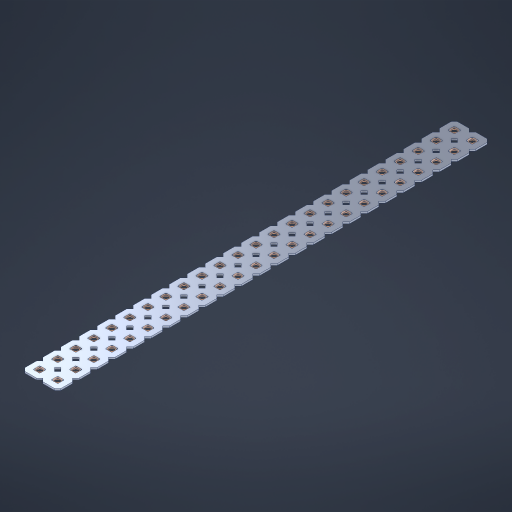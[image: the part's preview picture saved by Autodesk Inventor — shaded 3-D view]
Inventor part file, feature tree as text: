
AUTODESK INVENTOR PART (.ipt)
format: ipt  version: 2023 (Build 270158000, 158)  size: 814,080 bytes
history: native  units: in
note: dims shown in document units (in); Inventor stores cm internally (conversion verified against a paired STEP export)
features: other x49, extrude x47, sketch x2, pattern_linear x1
ambient origin geometry x8: Origin, YZ Plane, XZ Plane, XY Plane, X Axis, Y Axis, Z Axis, Center Point
bodies: Solid1 (feature_tree), Body (feature_tree)
feature tree (99):
  pattern_linear  "Rectangular Pattern1"  Spacing1=0.09in  [1 undecoded]
  sketch  "Sketch1"  dims[d1=0.5in]
  sketch  "Sketch2"  dims[d2=0.182in d3=0.09in d4=0.09in d5=0.09in d6=0.09in d7=0.09in d8=0.09in d9=0.09in d10=0.09in d11=0.02in d13=0.0in d14=0.172in d15=0.0625in d16=0.0in d19=0.5in d22=0.5in]
  other  "Srf1"
  other  "Srf126"
  other  "Srf127"
  other  "Srf128"
  other  "Srf129"
  other  "Srf130"
  other  "Srf131"
  other  "Srf250"
  other  "Srf251"
  other  "Srf252"
  other  "Srf253"
  other  "Srf254"
  other  "Srf255"
  other  "Srf256"
  other  "Srf257"
  other  "Srf258"
  other  "Srf259"
  other  "Srf260"
  other  "Srf261"
  other  "Srf262"
  other  "Srf263"
  other  "Srf264"
  other  "Srf265"
  other  "Srf266"
  other  "Srf268"
  other  "Srf269"
  other  "Srf270"
  other  "Srf271"
  other  "Srf272"
  other  "Srf273"
  other  "Srf274"
  other  "Srf275"
  other  "Srf276"
  other  "Srf277"
  other  "Srf278"
  other  "Srf279"
  other  "Srf280"
  other  "Srf281"
  other  "Srf282"
  other  "Srf283"
  other  "Srf284"
  other  "Srf285"
  other  "Srf286"
  other  "Srf287"
  other  "Srf288"
  other  "Srf289"
  other  "Srf290"
  other  "Srf291"
  other  "Circle"
  extrude  "ExtrusionSrf126"  Depth=0.09in
  extrude  "ExtrusionSrf127"  Depth=0.09in
  extrude  "ExtrusionSrf128"  Depth=0.09in
  extrude  "ExtrusionSrf129"  Depth=0.09in
  extrude  "ExtrusionSrf130"  Depth=0.09in
  extrude  "ExtrusionSrf131"  Depth=0.09in
  extrude  "ExtrusionSrf250"  Depth=0.09in
  extrude  "ExtrusionSrf251"  Depth=0.02in
  extrude  "ExtrusionSrf252"  TaperAngle=0.0deg  [1 undecoded]
  extrude  "ExtrusionSrf253"  Depth=0.5in
  extrude  "ExtrusionSrf254"  Depth=0.5in TaperAngle=0.0deg
  extrude  "ExtrusionSrf255"  Depth=0.5in
  extrude  "ExtrusionSrf256"  Depth=0.5in
  extrude  "ExtrusionSrf257"  [1 undecoded]
  extrude  "ExtrusionSrf258"  [1 undecoded]
  extrude  "ExtrusionSrf259"  [1 undecoded]
  extrude  "ExtrusionSrf260"  [1 undecoded]
  extrude  "ExtrusionSrf261"  [1 undecoded]
  extrude  "ExtrusionSrf262"  [1 undecoded]
  extrude  "ExtrusionSrf263"  [1 undecoded]
  extrude  "ExtrusionSrf264"  [1 undecoded]
  extrude  "ExtrusionSrf265"  [1 undecoded]
  extrude  "ExtrusionSrf266"  [1 undecoded]
  extrude  "ExtrusionSrf268"  [1 undecoded]
  extrude  "ExtrusionSrf269"  [1 undecoded]
  extrude  "ExtrusionSrf270"  [1 undecoded]
  extrude  "ExtrusionSrf271"  [1 undecoded]
  extrude  "ExtrusionSrf272"  [1 undecoded]
  extrude  "ExtrusionSrf273"  [1 undecoded]
  extrude  "ExtrusionSrf274"  [1 undecoded]
  extrude  "ExtrusionSrf275"  [1 undecoded]
  extrude  "ExtrusionSrf276"  [1 undecoded]
  extrude  "ExtrusionSrf277"  [1 undecoded]
  extrude  "ExtrusionSrf278"  [1 undecoded]
  extrude  "ExtrusionSrf279"  [1 undecoded]
  extrude  "ExtrusionSrf280"  [1 undecoded]
  extrude  "ExtrusionSrf281"  [1 undecoded]
  extrude  "ExtrusionSrf282"  [1 undecoded]
  extrude  "ExtrusionSrf283"  [1 undecoded]
  extrude  "ExtrusionSrf284"  [1 undecoded]
  extrude  "ExtrusionSrf285"  [1 undecoded]
  extrude  "ExtrusionSrf286"  [1 undecoded]
  extrude  "ExtrusionSrf287"  [1 undecoded]
  extrude  "ExtrusionSrf288"  [1 undecoded]
  extrude  "ExtrusionSrf289"  [1 undecoded]
  extrude  "ExtrusionSrf290"  [1 undecoded]
  extrude  "ExtrusionSrf291"  [1 undecoded]
note: 36 required parameter values undecoded (feature->parameter linkage not recoverable at this tier; creation-order binding heuristic only, values carry confidence <= 0.55)
